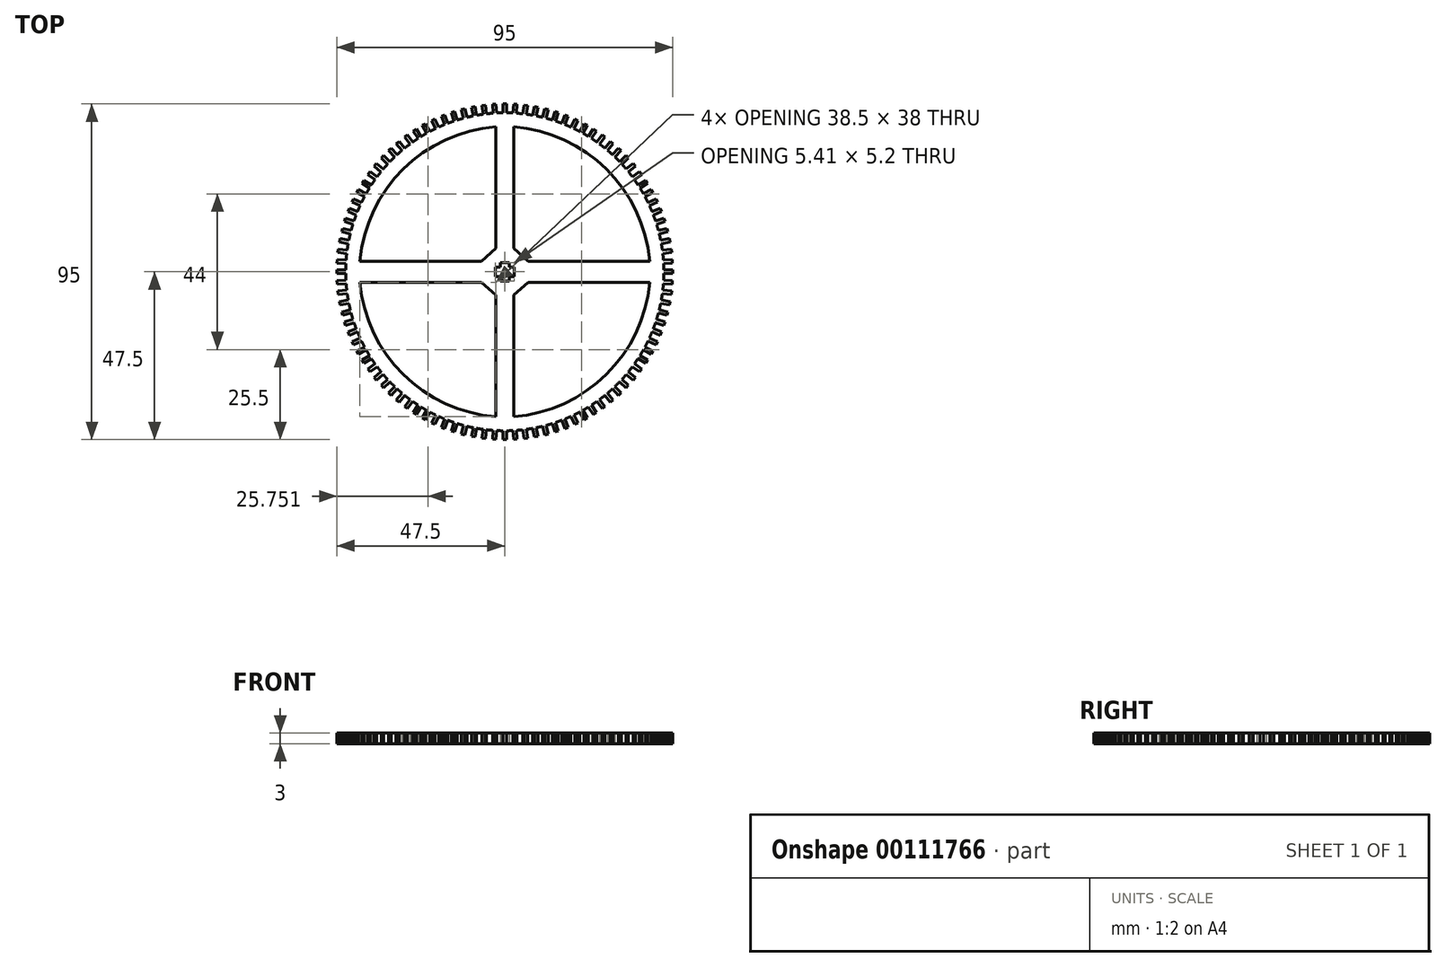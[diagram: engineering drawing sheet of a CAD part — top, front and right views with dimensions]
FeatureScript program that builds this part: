
annotation { "Feature Type Name" : "Feature", "Feature Type Description" : "" }
export const myFeature = defineFeature(function(context is Context, id is Id, definition is map)
    precondition{}
    {
        {
            var Q0;
            Q0=qCreatedBy(makeId("Top.planeOp"),FACE);
            var sketch = newSketch(context, id + "F0", { "sketchPlane" : qUnion([Q0])});
            skArc(sketch, "E0", {"start": v(-45, 0.5) * mm, "mid": v(-0.5, -45) * mm, "end": v(45, -0.5) * mm});
            skLineSegment(sketch, "E1.2.25.0", {"start": v(-47.5, 0.5) * mm, "end": v(-45, 0.5) * mm});
            skLineSegment(sketch, "E1.3.25.0", {"start": v(-47.5, -0.5) * mm, "end": v(-45, -0.5) * mm});
            skLineSegment(sketch, "E1.6.25.0", {"start": v(-47.5, 0) * mm, "end": v(-47.5, -0.5) * mm});
            skLineSegment(sketch, "E1.9.25.0", {"start": v(-47.5, 0) * mm, "end": v(-47.5, 0.5) * mm});
            skLineSegment(sketch, "E1.2.26.0", {"start": v(-47.44, -2.48) * mm, "end": v(-44.94, -2.33) * mm});
            skLineSegment(sketch, "E1.3.26.0", {"start": v(-47.37, -3.48) * mm, "end": v(-44.88, -3.32) * mm});
            skLineSegment(sketch, "E1.6.26.0", {"start": v(-47.4, -2.98) * mm, "end": v(-47.37, -3.48) * mm});
            skLineSegment(sketch, "E1.9.26.0", {"start": v(-47.4, -2.98) * mm, "end": v(-47.44, -2.48) * mm});
            skLineSegment(sketch, "E1.2.27.0", {"start": v(-47.19, -5.46) * mm, "end": v(-44.7, -5.14) * mm});
            skLineSegment(sketch, "E1.3.27.0", {"start": v(-47.06, -6.45) * mm, "end": v(-44.58, -6.14) * mm});
            skLineSegment(sketch, "E1.6.27.0", {"start": v(-47.13, -5.95) * mm, "end": v(-47.06, -6.45) * mm});
            skLineSegment(sketch, "E1.9.27.0", {"start": v(-47.13, -5.95) * mm, "end": v(-47.19, -5.46) * mm});
            skLineSegment(sketch, "E1.2.28.0", {"start": v(-46.75, -8.4) * mm, "end": v(-44.3, -7.94) * mm});
            skLineSegment(sketch, "E1.3.28.0", {"start": v(-46.56, -9.4) * mm, "end": v(-44.1, -8.92) * mm});
            skLineSegment(sketch, "E1.6.28.0", {"start": v(-46.66, -8.9) * mm, "end": v(-46.56, -9.4) * mm});
            skLineSegment(sketch, "E1.9.28.0", {"start": v(-46.66, -8.9) * mm, "end": v(-46.75, -8.4) * mm});
            skLineSegment(sketch, "E1.2.29.0", {"start": v(-46.13, -11.33) * mm, "end": v(-43.7, -10.7) * mm});
            skLineSegment(sketch, "E1.3.29.0", {"start": v(-45.88, -12.3) * mm, "end": v(-43.46, -11.67) * mm});
            skLineSegment(sketch, "E1.6.29.0", {"start": v(-46, -11.81) * mm, "end": v(-45.88, -12.3) * mm});
            skLineSegment(sketch, "E1.9.29.0", {"start": v(-46, -11.81) * mm, "end": v(-46.13, -11.33) * mm});
            skLineSegment(sketch, "E1.2.30.0", {"start": v(-45.33, -14.2) * mm, "end": v(-42.95, -13.43) * mm});
            skLineSegment(sketch, "E1.3.30.0", {"start": v(-45.02, -15.15) * mm, "end": v(-42.64, -14.38) * mm});
            skLineSegment(sketch, "E1.6.30.0", {"start": v(-45.18, -14.68) * mm, "end": v(-45.02, -15.15) * mm});
            skLineSegment(sketch, "E1.9.30.0", {"start": v(-45.18, -14.68) * mm, "end": v(-45.33, -14.2) * mm});
            skLineSegment(sketch, "E1.2.31.0", {"start": v(-44.35, -17.02) * mm, "end": v(-42.02, -16.1) * mm});
            skLineSegment(sketch, "E1.3.31.0", {"start": v(-43.98, -17.95) * mm, "end": v(-41.65, -17.03) * mm});
            skLineSegment(sketch, "E1.6.31.0", {"start": v(-44.16, -17.49) * mm, "end": v(-43.98, -17.95) * mm});
            skLineSegment(sketch, "E1.9.31.0", {"start": v(-44.16, -17.49) * mm, "end": v(-44.35, -17.02) * mm});
            skLineSegment(sketch, "E1.2.32.0", {"start": v(-43.2, -19.77) * mm, "end": v(-40.93, -18.7) * mm});
            skLineSegment(sketch, "E1.3.32.0", {"start": v(-42.77, -20.68) * mm, "end": v(-40.5, -19.61) * mm});
            skLineSegment(sketch, "E1.6.32.0", {"start": v(-42.98, -20.22) * mm, "end": v(-42.77, -20.68) * mm});
            skLineSegment(sketch, "E1.9.32.0", {"start": v(-42.98, -20.22) * mm, "end": v(-43.2, -19.77) * mm});
            skLineSegment(sketch, "E1.2.33.0", {"start": v(-41.87, -22.45) * mm, "end": v(-39.67, -21.24) * mm});
            skLineSegment(sketch, "E1.3.33.0", {"start": v(-41.38, -23.32) * mm, "end": v(-39.2, -22.12) * mm});
            skLineSegment(sketch, "E1.6.33.0", {"start": v(-41.62, -22.88) * mm, "end": v(-41.38, -23.32) * mm});
            skLineSegment(sketch, "E1.9.33.0", {"start": v(-41.62, -22.88) * mm, "end": v(-41.87, -22.45) * mm});
            skLineSegment(sketch, "E1.2.34.0", {"start": v(-40.37, -25.03) * mm, "end": v(-38.26, -23.69) * mm});
            skLineSegment(sketch, "E1.3.34.0", {"start": v(-39.84, -25.87) * mm, "end": v(-37.72, -24.53) * mm});
            skLineSegment(sketch, "E1.6.34.0", {"start": v(-40.1, -25.45) * mm, "end": v(-39.84, -25.87) * mm});
            skLineSegment(sketch, "E1.9.34.0", {"start": v(-40.1, -25.45) * mm, "end": v(-40.37, -25.03) * mm});
            skLineSegment(sketch, "E1.2.35.0", {"start": v(-38.72, -27.52) * mm, "end": v(-36.7, -26.04) * mm});
            skLineSegment(sketch, "E1.3.35.0", {"start": v(-38.13, -28.32) * mm, "end": v(-36.1, -26.85) * mm});
            skLineSegment(sketch, "E1.6.35.0", {"start": v(-38.43, -27.92) * mm, "end": v(-38.13, -28.32) * mm});
            skLineSegment(sketch, "E1.9.35.0", {"start": v(-38.43, -27.92) * mm, "end": v(-38.72, -27.52) * mm});
            skLineSegment(sketch, "E1.2.36.0", {"start": v(-36.92, -29.9) * mm, "end": v(-34.99, -28.3) * mm});
            skLineSegment(sketch, "E1.3.36.0", {"start": v(-36.28, -30.66) * mm, "end": v(-34.35, -29.07) * mm});
            skLineSegment(sketch, "E1.6.36.0", {"start": v(-36.6, -30.28) * mm, "end": v(-36.28, -30.66) * mm});
            skLineSegment(sketch, "E1.9.36.0", {"start": v(-36.6, -30.28) * mm, "end": v(-36.92, -29.9) * mm});
            skLineSegment(sketch, "E1.2.37.0", {"start": v(-34.97, -32.15) * mm, "end": v(-33.14, -30.44) * mm});
            skLineSegment(sketch, "E1.3.37.0", {"start": v(-34.28, -32.88) * mm, "end": v(-32.46, -31.17) * mm});
            skLineSegment(sketch, "E1.6.37.0", {"start": v(-34.63, -32.52) * mm, "end": v(-34.28, -32.88) * mm});
            skLineSegment(sketch, "E1.9.37.0", {"start": v(-34.63, -32.52) * mm, "end": v(-34.97, -32.15) * mm});
            skLineSegment(sketch, "E1.2.38.0", {"start": v(-32.88, -34.28) * mm, "end": v(-31.17, -32.46) * mm});
            skLineSegment(sketch, "E1.3.38.0", {"start": v(-32.15, -34.97) * mm, "end": v(-30.44, -33.14) * mm});
            skLineSegment(sketch, "E1.6.38.0", {"start": v(-32.52, -34.63) * mm, "end": v(-32.15, -34.97) * mm});
            skLineSegment(sketch, "E1.9.38.0", {"start": v(-32.52, -34.63) * mm, "end": v(-32.88, -34.28) * mm});
            skLineSegment(sketch, "E1.2.39.0", {"start": v(-30.66, -36.28) * mm, "end": v(-29.07, -34.35) * mm});
            skLineSegment(sketch, "E1.3.39.0", {"start": v(-29.9, -36.92) * mm, "end": v(-28.3, -34.99) * mm});
            skLineSegment(sketch, "E1.6.39.0", {"start": v(-30.28, -36.6) * mm, "end": v(-29.9, -36.92) * mm});
            skLineSegment(sketch, "E1.9.39.0", {"start": v(-30.28, -36.6) * mm, "end": v(-30.66, -36.28) * mm});
            skLineSegment(sketch, "E1.2.40.0", {"start": v(-28.32, -38.13) * mm, "end": v(-26.85, -36.1) * mm});
            skLineSegment(sketch, "E1.3.40.0", {"start": v(-27.52, -38.72) * mm, "end": v(-26.04, -36.7) * mm});
            skLineSegment(sketch, "E1.6.40.0", {"start": v(-27.92, -38.43) * mm, "end": v(-27.52, -38.72) * mm});
            skLineSegment(sketch, "E1.9.40.0", {"start": v(-27.92, -38.43) * mm, "end": v(-28.32, -38.13) * mm});
            skLineSegment(sketch, "E1.2.41.0", {"start": v(-25.87, -39.84) * mm, "end": v(-24.53, -37.72) * mm});
            skLineSegment(sketch, "E1.3.41.0", {"start": v(-25.03, -40.37) * mm, "end": v(-23.69, -38.26) * mm});
            skLineSegment(sketch, "E1.6.41.0", {"start": v(-25.45, -40.1) * mm, "end": v(-25.03, -40.37) * mm});
            skLineSegment(sketch, "E1.9.41.0", {"start": v(-25.45, -40.1) * mm, "end": v(-25.87, -39.84) * mm});
            skLineSegment(sketch, "E1.2.42.0", {"start": v(-23.32, -41.38) * mm, "end": v(-22.12, -39.2) * mm});
            skLineSegment(sketch, "E1.3.42.0", {"start": v(-22.45, -41.87) * mm, "end": v(-21.24, -39.67) * mm});
            skLineSegment(sketch, "E1.6.42.0", {"start": v(-22.88, -41.62) * mm, "end": v(-22.45, -41.87) * mm});
            skLineSegment(sketch, "E1.9.42.0", {"start": v(-22.88, -41.62) * mm, "end": v(-23.32, -41.38) * mm});
            skLineSegment(sketch, "E1.2.43.0", {"start": v(-20.68, -42.77) * mm, "end": v(-19.61, -40.5) * mm});
            skLineSegment(sketch, "E1.3.43.0", {"start": v(-19.77, -43.2) * mm, "end": v(-18.7, -40.93) * mm});
            skLineSegment(sketch, "E1.6.43.0", {"start": v(-20.22, -42.98) * mm, "end": v(-19.77, -43.2) * mm});
            skLineSegment(sketch, "E1.9.43.0", {"start": v(-20.22, -42.98) * mm, "end": v(-20.68, -42.77) * mm});
            skLineSegment(sketch, "E1.2.44.0", {"start": v(-17.95, -43.98) * mm, "end": v(-17.03, -41.65) * mm});
            skLineSegment(sketch, "E1.3.44.0", {"start": v(-17.02, -44.35) * mm, "end": v(-16.1, -42.02) * mm});
            skLineSegment(sketch, "E1.6.44.0", {"start": v(-17.49, -44.16) * mm, "end": v(-17.02, -44.35) * mm});
            skLineSegment(sketch, "E1.9.44.0", {"start": v(-17.49, -44.16) * mm, "end": v(-17.95, -43.98) * mm});
            skLineSegment(sketch, "E1.2.45.0", {"start": v(-15.15, -45.02) * mm, "end": v(-14.38, -42.64) * mm});
            skLineSegment(sketch, "E1.3.45.0", {"start": v(-14.2, -45.33) * mm, "end": v(-13.43, -42.95) * mm});
            skLineSegment(sketch, "E1.6.45.0", {"start": v(-14.68, -45.18) * mm, "end": v(-14.2, -45.33) * mm});
            skLineSegment(sketch, "E1.9.45.0", {"start": v(-14.68, -45.18) * mm, "end": v(-15.15, -45.02) * mm});
            skLineSegment(sketch, "E1.2.46.0", {"start": v(-12.3, -45.88) * mm, "end": v(-11.67, -43.46) * mm});
            skLineSegment(sketch, "E1.3.46.0", {"start": v(-11.33, -46.13) * mm, "end": v(-10.7, -43.7) * mm});
            skLineSegment(sketch, "E1.6.46.0", {"start": v(-11.81, -46) * mm, "end": v(-11.33, -46.13) * mm});
            skLineSegment(sketch, "E1.9.46.0", {"start": v(-11.81, -46) * mm, "end": v(-12.3, -45.88) * mm});
            skLineSegment(sketch, "E1.2.47.0", {"start": v(-9.4, -46.56) * mm, "end": v(-8.92, -44.1) * mm});
            skLineSegment(sketch, "E1.3.47.0", {"start": v(-8.4, -46.75) * mm, "end": v(-7.94, -44.3) * mm});
            skLineSegment(sketch, "E1.6.47.0", {"start": v(-8.9, -46.66) * mm, "end": v(-8.4, -46.75) * mm});
            skLineSegment(sketch, "E1.9.47.0", {"start": v(-8.9, -46.66) * mm, "end": v(-9.4, -46.56) * mm});
            skLineSegment(sketch, "E1.2.48.0", {"start": v(-6.45, -47.06) * mm, "end": v(-6.14, -44.58) * mm});
            skLineSegment(sketch, "E1.3.48.0", {"start": v(-5.46, -47.19) * mm, "end": v(-5.14, -44.7) * mm});
            skLineSegment(sketch, "E1.6.48.0", {"start": v(-5.95, -47.13) * mm, "end": v(-5.46, -47.19) * mm});
            skLineSegment(sketch, "E1.9.48.0", {"start": v(-5.95, -47.13) * mm, "end": v(-6.45, -47.06) * mm});
            skLineSegment(sketch, "E1.2.49.0", {"start": v(-3.48, -47.37) * mm, "end": v(-3.32, -44.88) * mm});
            skLineSegment(sketch, "E1.3.49.0", {"start": v(-2.48, -47.44) * mm, "end": v(-2.33, -44.94) * mm});
            skLineSegment(sketch, "E1.6.49.0", {"start": v(-2.98, -47.4) * mm, "end": v(-2.48, -47.44) * mm});
            skLineSegment(sketch, "E1.9.49.0", {"start": v(-2.98, -47.4) * mm, "end": v(-3.48, -47.37) * mm});
            skLineSegment(sketch, "E1.2.50.0", {"start": v(-0.5, -47.5) * mm, "end": v(-0.5, -45) * mm});
            skLineSegment(sketch, "E1.3.50.0", {"start": v(0.5, -47.5) * mm, "end": v(0.5, -45) * mm});
            skLineSegment(sketch, "E1.6.50.0", {"start": v(0, -47.5) * mm, "end": v(0.5, -47.5) * mm});
            skLineSegment(sketch, "E1.9.50.0", {"start": v(0, -47.5) * mm, "end": v(-0.5, -47.5) * mm});
            skLineSegment(sketch, "E1.2.51.0", {"start": v(2.48, -47.44) * mm, "end": v(2.33, -44.94) * mm});
            skLineSegment(sketch, "E1.3.51.0", {"start": v(3.48, -47.37) * mm, "end": v(3.32, -44.88) * mm});
            skLineSegment(sketch, "E1.6.51.0", {"start": v(2.98, -47.4) * mm, "end": v(3.48, -47.37) * mm});
            skLineSegment(sketch, "E1.9.51.0", {"start": v(2.98, -47.4) * mm, "end": v(2.48, -47.44) * mm});
            skLineSegment(sketch, "E1.2.52.0", {"start": v(5.46, -47.19) * mm, "end": v(5.14, -44.7) * mm});
            skLineSegment(sketch, "E1.3.52.0", {"start": v(6.45, -47.06) * mm, "end": v(6.14, -44.58) * mm});
            skLineSegment(sketch, "E1.6.52.0", {"start": v(5.95, -47.13) * mm, "end": v(6.45, -47.06) * mm});
            skLineSegment(sketch, "E1.9.52.0", {"start": v(5.95, -47.13) * mm, "end": v(5.46, -47.19) * mm});
            skLineSegment(sketch, "E1.2.53.0", {"start": v(8.4, -46.75) * mm, "end": v(7.94, -44.3) * mm});
            skLineSegment(sketch, "E1.3.53.0", {"start": v(9.4, -46.56) * mm, "end": v(8.92, -44.1) * mm});
            skLineSegment(sketch, "E1.6.53.0", {"start": v(8.9, -46.66) * mm, "end": v(9.4, -46.56) * mm});
            skLineSegment(sketch, "E1.9.53.0", {"start": v(8.9, -46.66) * mm, "end": v(8.4, -46.75) * mm});
            skLineSegment(sketch, "E1.2.54.0", {"start": v(11.33, -46.13) * mm, "end": v(10.7, -43.7) * mm});
            skLineSegment(sketch, "E1.3.54.0", {"start": v(12.3, -45.88) * mm, "end": v(11.67, -43.46) * mm});
            skLineSegment(sketch, "E1.6.54.0", {"start": v(11.81, -46) * mm, "end": v(12.3, -45.88) * mm});
            skLineSegment(sketch, "E1.9.54.0", {"start": v(11.81, -46) * mm, "end": v(11.33, -46.13) * mm});
            skLineSegment(sketch, "E1.2.55.0", {"start": v(14.2, -45.33) * mm, "end": v(13.43, -42.95) * mm});
            skLineSegment(sketch, "E1.3.55.0", {"start": v(15.15, -45.02) * mm, "end": v(14.38, -42.64) * mm});
            skLineSegment(sketch, "E1.6.55.0", {"start": v(14.68, -45.18) * mm, "end": v(15.15, -45.02) * mm});
            skLineSegment(sketch, "E1.9.55.0", {"start": v(14.68, -45.18) * mm, "end": v(14.2, -45.33) * mm});
            skLineSegment(sketch, "E1.2.56.0", {"start": v(17.02, -44.35) * mm, "end": v(16.1, -42.02) * mm});
            skLineSegment(sketch, "E1.3.56.0", {"start": v(17.95, -43.98) * mm, "end": v(17.03, -41.65) * mm});
            skLineSegment(sketch, "E1.6.56.0", {"start": v(17.49, -44.16) * mm, "end": v(17.95, -43.98) * mm});
            skLineSegment(sketch, "E1.9.56.0", {"start": v(17.49, -44.16) * mm, "end": v(17.02, -44.35) * mm});
            skLineSegment(sketch, "E1.2.57.0", {"start": v(19.77, -43.2) * mm, "end": v(18.7, -40.93) * mm});
            skLineSegment(sketch, "E1.3.57.0", {"start": v(20.68, -42.77) * mm, "end": v(19.61, -40.5) * mm});
            skLineSegment(sketch, "E1.6.57.0", {"start": v(20.22, -42.98) * mm, "end": v(20.68, -42.77) * mm});
            skLineSegment(sketch, "E1.9.57.0", {"start": v(20.22, -42.98) * mm, "end": v(19.77, -43.2) * mm});
            skLineSegment(sketch, "E1.2.58.0", {"start": v(22.45, -41.87) * mm, "end": v(21.24, -39.67) * mm});
            skLineSegment(sketch, "E1.3.58.0", {"start": v(23.32, -41.38) * mm, "end": v(22.12, -39.2) * mm});
            skLineSegment(sketch, "E1.6.58.0", {"start": v(22.88, -41.62) * mm, "end": v(23.32, -41.38) * mm});
            skLineSegment(sketch, "E1.9.58.0", {"start": v(22.88, -41.62) * mm, "end": v(22.45, -41.87) * mm});
            skLineSegment(sketch, "E1.2.59.0", {"start": v(25.03, -40.37) * mm, "end": v(23.69, -38.26) * mm});
            skLineSegment(sketch, "E1.3.59.0", {"start": v(25.87, -39.84) * mm, "end": v(24.53, -37.72) * mm});
            skLineSegment(sketch, "E1.6.59.0", {"start": v(25.45, -40.1) * mm, "end": v(25.87, -39.84) * mm});
            skLineSegment(sketch, "E1.9.59.0", {"start": v(25.45, -40.1) * mm, "end": v(25.03, -40.37) * mm});
            skLineSegment(sketch, "E1.2.60.0", {"start": v(27.52, -38.72) * mm, "end": v(26.04, -36.7) * mm});
            skLineSegment(sketch, "E1.3.60.0", {"start": v(28.32, -38.13) * mm, "end": v(26.85, -36.1) * mm});
            skLineSegment(sketch, "E1.6.60.0", {"start": v(27.92, -38.43) * mm, "end": v(28.32, -38.13) * mm});
            skLineSegment(sketch, "E1.9.60.0", {"start": v(27.92, -38.43) * mm, "end": v(27.52, -38.72) * mm});
            skLineSegment(sketch, "E1.2.61.0", {"start": v(29.9, -36.92) * mm, "end": v(28.3, -34.99) * mm});
            skLineSegment(sketch, "E1.3.61.0", {"start": v(30.66, -36.28) * mm, "end": v(29.07, -34.35) * mm});
            skLineSegment(sketch, "E1.6.61.0", {"start": v(30.28, -36.6) * mm, "end": v(30.66, -36.28) * mm});
            skLineSegment(sketch, "E1.9.61.0", {"start": v(30.28, -36.6) * mm, "end": v(29.9, -36.92) * mm});
            skLineSegment(sketch, "E1.2.62.0", {"start": v(32.15, -34.97) * mm, "end": v(30.44, -33.14) * mm});
            skLineSegment(sketch, "E1.3.62.0", {"start": v(32.88, -34.28) * mm, "end": v(31.17, -32.46) * mm});
            skLineSegment(sketch, "E1.6.62.0", {"start": v(32.52, -34.63) * mm, "end": v(32.88, -34.28) * mm});
            skLineSegment(sketch, "E1.9.62.0", {"start": v(32.52, -34.63) * mm, "end": v(32.15, -34.97) * mm});
            skLineSegment(sketch, "E1.2.63.0", {"start": v(34.28, -32.88) * mm, "end": v(32.46, -31.17) * mm});
            skLineSegment(sketch, "E1.3.63.0", {"start": v(34.97, -32.15) * mm, "end": v(33.14, -30.44) * mm});
            skLineSegment(sketch, "E1.6.63.0", {"start": v(34.63, -32.52) * mm, "end": v(34.97, -32.15) * mm});
            skLineSegment(sketch, "E1.9.63.0", {"start": v(34.63, -32.52) * mm, "end": v(34.28, -32.88) * mm});
            skLineSegment(sketch, "E1.2.64.0", {"start": v(36.28, -30.66) * mm, "end": v(34.35, -29.07) * mm});
            skLineSegment(sketch, "E1.3.64.0", {"start": v(36.92, -29.9) * mm, "end": v(34.99, -28.3) * mm});
            skLineSegment(sketch, "E1.6.64.0", {"start": v(36.6, -30.28) * mm, "end": v(36.92, -29.9) * mm});
            skLineSegment(sketch, "E1.9.64.0", {"start": v(36.6, -30.28) * mm, "end": v(36.28, -30.66) * mm});
            skLineSegment(sketch, "E1.2.65.0", {"start": v(38.13, -28.32) * mm, "end": v(36.1, -26.85) * mm});
            skLineSegment(sketch, "E1.3.65.0", {"start": v(38.72, -27.52) * mm, "end": v(36.7, -26.04) * mm});
            skLineSegment(sketch, "E1.6.65.0", {"start": v(38.43, -27.92) * mm, "end": v(38.72, -27.52) * mm});
            skLineSegment(sketch, "E1.9.65.0", {"start": v(38.43, -27.92) * mm, "end": v(38.13, -28.32) * mm});
            skLineSegment(sketch, "E1.2.66.0", {"start": v(39.84, -25.87) * mm, "end": v(37.72, -24.53) * mm});
            skLineSegment(sketch, "E1.3.66.0", {"start": v(40.37, -25.03) * mm, "end": v(38.26, -23.69) * mm});
            skLineSegment(sketch, "E1.6.66.0", {"start": v(40.1, -25.45) * mm, "end": v(40.37, -25.03) * mm});
            skLineSegment(sketch, "E1.9.66.0", {"start": v(40.1, -25.45) * mm, "end": v(39.84, -25.87) * mm});
            skLineSegment(sketch, "E1.2.67.0", {"start": v(41.38, -23.32) * mm, "end": v(39.2, -22.12) * mm});
            skLineSegment(sketch, "E1.3.67.0", {"start": v(41.87, -22.45) * mm, "end": v(39.67, -21.24) * mm});
            skLineSegment(sketch, "E1.6.67.0", {"start": v(41.62, -22.88) * mm, "end": v(41.87, -22.45) * mm});
            skLineSegment(sketch, "E1.9.67.0", {"start": v(41.62, -22.88) * mm, "end": v(41.38, -23.32) * mm});
            skLineSegment(sketch, "E1.2.68.0", {"start": v(42.77, -20.68) * mm, "end": v(40.5, -19.61) * mm});
            skLineSegment(sketch, "E1.3.68.0", {"start": v(43.2, -19.77) * mm, "end": v(40.93, -18.7) * mm});
            skLineSegment(sketch, "E1.6.68.0", {"start": v(42.98, -20.22) * mm, "end": v(43.2, -19.77) * mm});
            skLineSegment(sketch, "E1.9.68.0", {"start": v(42.98, -20.22) * mm, "end": v(42.77, -20.68) * mm});
            skLineSegment(sketch, "E1.2.69.0", {"start": v(43.98, -17.95) * mm, "end": v(41.65, -17.03) * mm});
            skLineSegment(sketch, "E1.3.69.0", {"start": v(44.35, -17.02) * mm, "end": v(42.02, -16.1) * mm});
            skLineSegment(sketch, "E1.6.69.0", {"start": v(44.16, -17.49) * mm, "end": v(44.35, -17.02) * mm});
            skLineSegment(sketch, "E1.9.69.0", {"start": v(44.16, -17.49) * mm, "end": v(43.98, -17.95) * mm});
            skLineSegment(sketch, "E1.2.70.0", {"start": v(45.02, -15.15) * mm, "end": v(42.64, -14.38) * mm});
            skLineSegment(sketch, "E1.3.70.0", {"start": v(45.33, -14.2) * mm, "end": v(42.95, -13.43) * mm});
            skLineSegment(sketch, "E1.6.70.0", {"start": v(45.18, -14.68) * mm, "end": v(45.33, -14.2) * mm});
            skLineSegment(sketch, "E1.9.70.0", {"start": v(45.18, -14.68) * mm, "end": v(45.02, -15.15) * mm});
            skLineSegment(sketch, "E1.2.71.0", {"start": v(45.88, -12.3) * mm, "end": v(43.46, -11.67) * mm});
            skLineSegment(sketch, "E1.3.71.0", {"start": v(46.13, -11.33) * mm, "end": v(43.7, -10.7) * mm});
            skLineSegment(sketch, "E1.6.71.0", {"start": v(46, -11.81) * mm, "end": v(46.13, -11.33) * mm});
            skLineSegment(sketch, "E1.9.71.0", {"start": v(46, -11.81) * mm, "end": v(45.88, -12.3) * mm});
            skLineSegment(sketch, "E1.2.72.0", {"start": v(46.56, -9.4) * mm, "end": v(44.1, -8.92) * mm});
            skLineSegment(sketch, "E1.3.72.0", {"start": v(46.75, -8.4) * mm, "end": v(44.3, -7.94) * mm});
            skLineSegment(sketch, "E1.6.72.0", {"start": v(46.66, -8.9) * mm, "end": v(46.75, -8.4) * mm});
            skLineSegment(sketch, "E1.9.72.0", {"start": v(46.66, -8.9) * mm, "end": v(46.56, -9.4) * mm});
            skLineSegment(sketch, "E1.2.73.0", {"start": v(47.06, -6.45) * mm, "end": v(44.58, -6.14) * mm});
            skLineSegment(sketch, "E1.3.73.0", {"start": v(47.19, -5.46) * mm, "end": v(44.7, -5.14) * mm});
            skLineSegment(sketch, "E1.6.73.0", {"start": v(47.13, -5.95) * mm, "end": v(47.19, -5.46) * mm});
            skLineSegment(sketch, "E1.9.73.0", {"start": v(47.13, -5.95) * mm, "end": v(47.06, -6.45) * mm});
            skLineSegment(sketch, "E1.2.74.0", {"start": v(47.37, -3.48) * mm, "end": v(44.88, -3.32) * mm});
            skLineSegment(sketch, "E1.3.74.0", {"start": v(47.44, -2.48) * mm, "end": v(44.94, -2.33) * mm});
            skLineSegment(sketch, "E1.6.74.0", {"start": v(47.4, -2.98) * mm, "end": v(47.44, -2.48) * mm});
            skLineSegment(sketch, "E1.9.74.0", {"start": v(47.4, -2.98) * mm, "end": v(47.37, -3.48) * mm});
            skLineSegment(sketch, "E2.MirrorCS", {"start": v(-6.6, -3) * mm, "end": v(-41, -3) * mm});
            skLineSegment(sketch, "E3.MirrorCS", {"start": v(-2.5, -6.6) * mm, "end": v(-6.6, -3) * mm});
            skLineSegment(sketch, "E4.MirrorCS", {"start": v(-2.5, -6.6) * mm, "end": v(-2.5, -41) * mm});
            skArc(sketch, "E5.MirrorCS", {"start": v(-41, -3) * mm, "mid": v(-28.72, -29.07) * mm, "end": v(-2.5, -41) * mm});
            skLineSegment(sketch, "E6.MirrorCS", {"start": v(2.5, -6.6) * mm, "end": v(2.5, -41) * mm});
            skLineSegment(sketch, "E7.MirrorCS", {"start": v(2.5, -6.6) * mm, "end": v(6.6, -3) * mm});
            skLineSegment(sketch, "E8.MirrorCS", {"start": v(6.6, -3) * mm, "end": v(41, -3) * mm});
            skArc(sketch, "E9.MirrorCS", {"start": v(41, -3) * mm, "mid": v(28.72, -29.07) * mm, "end": v(2.5, -41) * mm});
            skArc(sketch, "E10", {"start": v(-4, 0) * mm, "mid": v(0, -4) * mm, "end": v(4, 0) * mm});
            skLineSegment(sketch, "E11", {"start": v(-4, 0) * mm, "end": v(-16, 0) * mm});
            skLineSegment(sketch, "E12", {"start": v(-16, 0) * mm, "end": v(-15.27, -1.74) * mm});
            skLineSegment(sketch, "E13", {"start": v(-15.27, -1.74) * mm, "end": v(-26.47, -1.74) * mm});
            skLineSegment(sketch, "E14", {"start": v(-45, 0.5) * mm, "end": v(-25.37, 0) * mm});
            skLineSegment(sketch, "E15", {"start": v(-25.37, 0) * mm, "end": v(-26.47, -1.74) * mm});
            skLineSegment(sketch, "E16", {"start": v(45, -0.5) * mm, "end": v(34.22, 0) * mm});
            skLineSegment(sketch, "E17", {"start": v(34.22, 0) * mm, "end": v(35.03, -1.4) * mm});
            skLineSegment(sketch, "E18", {"start": v(35.03, -1.4) * mm, "end": v(24.89, -1.4) * mm});
            skLineSegment(sketch, "E19", {"start": v(24.89, -1.4) * mm, "end": v(26.1, 0) * mm});
            skLineSegment(sketch, "E20", {"start": v(26.1, 0) * mm, "end": v(4, 0) * mm});
            skCircle(sketch, "E21", {"center": v(0, 0) * mm, "radius": 45 * mm});
            skLineSegment(sketch, "E22.MirrorCS", {"start": v(-6.6, 3) * mm, "end": v(-41, 3) * mm});
            skLineSegment(sketch, "E23.MirrorCS", {"start": v(-2.5, 6.6) * mm, "end": v(-6.6, 3) * mm});
            skLineSegment(sketch, "E24.MirrorCS", {"start": v(-2.5, 6.6) * mm, "end": v(-2.5, 41) * mm});
            skArc(sketch, "E25.MirrorCS", {"start": v(-41, 3) * mm, "mid": v(-28.72, 29.07) * mm, "end": v(-2.5, 41) * mm});
            skLineSegment(sketch, "E26.MirrorCS", {"start": v(2.5, 6.6) * mm, "end": v(2.5, 41) * mm});
            skArc(sketch, "E27.MirrorCS", {"start": v(41, 3) * mm, "mid": v(28.72, 29.07) * mm, "end": v(2.5, 41) * mm});
            skLineSegment(sketch, "E28.MirrorCS", {"start": v(6.6, 3) * mm, "end": v(41, 3) * mm});
            skLineSegment(sketch, "E29.MirrorCS", {"start": v(2.5, 6.6) * mm, "end": v(6.6, 3) * mm});
            skLineSegment(sketch, "E30.1.50.0", {"start": v(47.5, 0.5) * mm, "end": v(45, 0.5) * mm});
            skLineSegment(sketch, "E30.3.50.0", {"start": v(47.5, -0.5) * mm, "end": v(45, -0.5) * mm});
            skLineSegment(sketch, "E30.6.50.0", {"start": v(47.5, 0) * mm, "end": v(47.5, -0.5) * mm});
            skLineSegment(sketch, "E30.9.50.0", {"start": v(47.5, 0) * mm, "end": v(47.5, 0.5) * mm});
            skLineSegment(sketch, "E30.1.51.0", {"start": v(47.37, 3.48) * mm, "end": v(44.88, 3.32) * mm});
            skLineSegment(sketch, "E30.3.51.0", {"start": v(47.44, 2.48) * mm, "end": v(44.94, 2.33) * mm});
            skLineSegment(sketch, "E30.6.51.0", {"start": v(47.4, 2.98) * mm, "end": v(47.44, 2.48) * mm});
            skLineSegment(sketch, "E30.9.51.0", {"start": v(47.4, 2.98) * mm, "end": v(47.37, 3.48) * mm});
            skLineSegment(sketch, "E30.1.52.0", {"start": v(47.06, 6.45) * mm, "end": v(44.58, 6.14) * mm});
            skLineSegment(sketch, "E30.3.52.0", {"start": v(47.19, 5.46) * mm, "end": v(44.7, 5.14) * mm});
            skLineSegment(sketch, "E30.6.52.0", {"start": v(47.13, 5.95) * mm, "end": v(47.19, 5.46) * mm});
            skLineSegment(sketch, "E30.9.52.0", {"start": v(47.13, 5.95) * mm, "end": v(47.06, 6.45) * mm});
            skLineSegment(sketch, "E30.1.53.0", {"start": v(46.56, 9.4) * mm, "end": v(44.1, 8.92) * mm});
            skLineSegment(sketch, "E30.3.53.0", {"start": v(46.75, 8.4) * mm, "end": v(44.3, 7.94) * mm});
            skLineSegment(sketch, "E30.6.53.0", {"start": v(46.66, 8.9) * mm, "end": v(46.75, 8.4) * mm});
            skLineSegment(sketch, "E30.9.53.0", {"start": v(46.66, 8.9) * mm, "end": v(46.56, 9.4) * mm});
            skLineSegment(sketch, "E30.1.54.0", {"start": v(45.88, 12.3) * mm, "end": v(43.46, 11.67) * mm});
            skLineSegment(sketch, "E30.3.54.0", {"start": v(46.13, 11.33) * mm, "end": v(43.7, 10.7) * mm});
            skLineSegment(sketch, "E30.6.54.0", {"start": v(46, 11.81) * mm, "end": v(46.13, 11.33) * mm});
            skLineSegment(sketch, "E30.9.54.0", {"start": v(46, 11.81) * mm, "end": v(45.88, 12.3) * mm});
            skLineSegment(sketch, "E30.1.55.0", {"start": v(45.02, 15.15) * mm, "end": v(42.64, 14.38) * mm});
            skLineSegment(sketch, "E30.3.55.0", {"start": v(45.33, 14.2) * mm, "end": v(42.95, 13.43) * mm});
            skLineSegment(sketch, "E30.6.55.0", {"start": v(45.18, 14.68) * mm, "end": v(45.33, 14.2) * mm});
            skLineSegment(sketch, "E30.9.55.0", {"start": v(45.18, 14.68) * mm, "end": v(45.02, 15.15) * mm});
            skLineSegment(sketch, "E30.1.56.0", {"start": v(43.98, 17.95) * mm, "end": v(41.65, 17.03) * mm});
            skLineSegment(sketch, "E30.3.56.0", {"start": v(44.35, 17.02) * mm, "end": v(42.02, 16.1) * mm});
            skLineSegment(sketch, "E30.6.56.0", {"start": v(44.16, 17.49) * mm, "end": v(44.35, 17.02) * mm});
            skLineSegment(sketch, "E30.9.56.0", {"start": v(44.16, 17.49) * mm, "end": v(43.98, 17.95) * mm});
            skLineSegment(sketch, "E30.1.57.0", {"start": v(42.77, 20.68) * mm, "end": v(40.5, 19.61) * mm});
            skLineSegment(sketch, "E30.3.57.0", {"start": v(43.2, 19.77) * mm, "end": v(40.93, 18.7) * mm});
            skLineSegment(sketch, "E30.6.57.0", {"start": v(42.98, 20.22) * mm, "end": v(43.2, 19.77) * mm});
            skLineSegment(sketch, "E30.9.57.0", {"start": v(42.98, 20.22) * mm, "end": v(42.77, 20.68) * mm});
            skLineSegment(sketch, "E30.1.58.0", {"start": v(41.38, 23.32) * mm, "end": v(39.2, 22.12) * mm});
            skLineSegment(sketch, "E30.3.58.0", {"start": v(41.87, 22.45) * mm, "end": v(39.67, 21.24) * mm});
            skLineSegment(sketch, "E30.6.58.0", {"start": v(41.62, 22.88) * mm, "end": v(41.87, 22.45) * mm});
            skLineSegment(sketch, "E30.9.58.0", {"start": v(41.62, 22.88) * mm, "end": v(41.38, 23.32) * mm});
            skLineSegment(sketch, "E30.1.59.0", {"start": v(39.84, 25.87) * mm, "end": v(37.72, 24.53) * mm});
            skLineSegment(sketch, "E30.3.59.0", {"start": v(40.37, 25.03) * mm, "end": v(38.26, 23.69) * mm});
            skLineSegment(sketch, "E30.6.59.0", {"start": v(40.1, 25.45) * mm, "end": v(40.37, 25.03) * mm});
            skLineSegment(sketch, "E30.9.59.0", {"start": v(40.1, 25.45) * mm, "end": v(39.84, 25.87) * mm});
            skLineSegment(sketch, "E30.1.60.0", {"start": v(38.13, 28.32) * mm, "end": v(36.1, 26.85) * mm});
            skLineSegment(sketch, "E30.3.60.0", {"start": v(38.72, 27.52) * mm, "end": v(36.7, 26.04) * mm});
            skLineSegment(sketch, "E30.6.60.0", {"start": v(38.43, 27.92) * mm, "end": v(38.72, 27.52) * mm});
            skLineSegment(sketch, "E30.9.60.0", {"start": v(38.43, 27.92) * mm, "end": v(38.13, 28.32) * mm});
            skLineSegment(sketch, "E30.1.61.0", {"start": v(36.28, 30.66) * mm, "end": v(34.35, 29.07) * mm});
            skLineSegment(sketch, "E30.3.61.0", {"start": v(36.92, 29.9) * mm, "end": v(34.99, 28.3) * mm});
            skLineSegment(sketch, "E30.6.61.0", {"start": v(36.6, 30.28) * mm, "end": v(36.92, 29.9) * mm});
            skLineSegment(sketch, "E30.9.61.0", {"start": v(36.6, 30.28) * mm, "end": v(36.28, 30.66) * mm});
            skLineSegment(sketch, "E30.1.62.0", {"start": v(34.28, 32.88) * mm, "end": v(32.46, 31.17) * mm});
            skLineSegment(sketch, "E30.3.62.0", {"start": v(34.97, 32.15) * mm, "end": v(33.14, 30.44) * mm});
            skLineSegment(sketch, "E30.6.62.0", {"start": v(34.63, 32.52) * mm, "end": v(34.97, 32.15) * mm});
            skLineSegment(sketch, "E30.9.62.0", {"start": v(34.63, 32.52) * mm, "end": v(34.28, 32.88) * mm});
            skLineSegment(sketch, "E30.1.63.0", {"start": v(32.15, 34.97) * mm, "end": v(30.44, 33.14) * mm});
            skLineSegment(sketch, "E30.3.63.0", {"start": v(32.88, 34.28) * mm, "end": v(31.17, 32.46) * mm});
            skLineSegment(sketch, "E30.6.63.0", {"start": v(32.52, 34.63) * mm, "end": v(32.88, 34.28) * mm});
            skLineSegment(sketch, "E30.9.63.0", {"start": v(32.52, 34.63) * mm, "end": v(32.15, 34.97) * mm});
            skLineSegment(sketch, "E30.1.64.0", {"start": v(29.9, 36.92) * mm, "end": v(28.3, 34.99) * mm});
            skLineSegment(sketch, "E30.3.64.0", {"start": v(30.66, 36.28) * mm, "end": v(29.07, 34.35) * mm});
            skLineSegment(sketch, "E30.6.64.0", {"start": v(30.28, 36.6) * mm, "end": v(30.66, 36.28) * mm});
            skLineSegment(sketch, "E30.9.64.0", {"start": v(30.28, 36.6) * mm, "end": v(29.9, 36.92) * mm});
            skLineSegment(sketch, "E30.1.65.0", {"start": v(27.52, 38.72) * mm, "end": v(26.04, 36.7) * mm});
            skLineSegment(sketch, "E30.3.65.0", {"start": v(28.32, 38.13) * mm, "end": v(26.85, 36.1) * mm});
            skLineSegment(sketch, "E30.6.65.0", {"start": v(27.92, 38.43) * mm, "end": v(28.32, 38.13) * mm});
            skLineSegment(sketch, "E30.9.65.0", {"start": v(27.92, 38.43) * mm, "end": v(27.52, 38.72) * mm});
            skLineSegment(sketch, "E30.1.66.0", {"start": v(25.03, 40.37) * mm, "end": v(23.69, 38.26) * mm});
            skLineSegment(sketch, "E30.3.66.0", {"start": v(25.87, 39.84) * mm, "end": v(24.53, 37.72) * mm});
            skLineSegment(sketch, "E30.6.66.0", {"start": v(25.45, 40.1) * mm, "end": v(25.87, 39.84) * mm});
            skLineSegment(sketch, "E30.9.66.0", {"start": v(25.45, 40.1) * mm, "end": v(25.03, 40.37) * mm});
            skLineSegment(sketch, "E30.1.67.0", {"start": v(22.45, 41.87) * mm, "end": v(21.24, 39.67) * mm});
            skLineSegment(sketch, "E30.3.67.0", {"start": v(23.32, 41.38) * mm, "end": v(22.12, 39.2) * mm});
            skLineSegment(sketch, "E30.6.67.0", {"start": v(22.88, 41.62) * mm, "end": v(23.32, 41.38) * mm});
            skLineSegment(sketch, "E30.9.67.0", {"start": v(22.88, 41.62) * mm, "end": v(22.45, 41.87) * mm});
            skLineSegment(sketch, "E30.1.68.0", {"start": v(19.77, 43.2) * mm, "end": v(18.7, 40.93) * mm});
            skLineSegment(sketch, "E30.3.68.0", {"start": v(20.68, 42.77) * mm, "end": v(19.61, 40.5) * mm});
            skLineSegment(sketch, "E30.6.68.0", {"start": v(20.22, 42.98) * mm, "end": v(20.68, 42.77) * mm});
            skLineSegment(sketch, "E30.9.68.0", {"start": v(20.22, 42.98) * mm, "end": v(19.77, 43.2) * mm});
            skLineSegment(sketch, "E30.1.69.0", {"start": v(17.02, 44.35) * mm, "end": v(16.1, 42.02) * mm});
            skLineSegment(sketch, "E30.3.69.0", {"start": v(17.95, 43.98) * mm, "end": v(17.03, 41.65) * mm});
            skLineSegment(sketch, "E30.6.69.0", {"start": v(17.49, 44.16) * mm, "end": v(17.95, 43.98) * mm});
            skLineSegment(sketch, "E30.9.69.0", {"start": v(17.49, 44.16) * mm, "end": v(17.02, 44.35) * mm});
            skLineSegment(sketch, "E30.1.70.0", {"start": v(14.2, 45.33) * mm, "end": v(13.43, 42.95) * mm});
            skLineSegment(sketch, "E30.3.70.0", {"start": v(15.15, 45.02) * mm, "end": v(14.38, 42.64) * mm});
            skLineSegment(sketch, "E30.6.70.0", {"start": v(14.68, 45.18) * mm, "end": v(15.15, 45.02) * mm});
            skLineSegment(sketch, "E30.9.70.0", {"start": v(14.68, 45.18) * mm, "end": v(14.2, 45.33) * mm});
            skLineSegment(sketch, "E30.1.71.0", {"start": v(11.33, 46.13) * mm, "end": v(10.7, 43.7) * mm});
            skLineSegment(sketch, "E30.3.71.0", {"start": v(12.3, 45.88) * mm, "end": v(11.67, 43.46) * mm});
            skLineSegment(sketch, "E30.6.71.0", {"start": v(11.81, 46) * mm, "end": v(12.3, 45.88) * mm});
            skLineSegment(sketch, "E30.9.71.0", {"start": v(11.81, 46) * mm, "end": v(11.33, 46.13) * mm});
            skLineSegment(sketch, "E30.1.72.0", {"start": v(8.4, 46.75) * mm, "end": v(7.94, 44.3) * mm});
            skLineSegment(sketch, "E30.3.72.0", {"start": v(9.4, 46.56) * mm, "end": v(8.92, 44.1) * mm});
            skLineSegment(sketch, "E30.6.72.0", {"start": v(8.9, 46.66) * mm, "end": v(9.4, 46.56) * mm});
            skLineSegment(sketch, "E30.9.72.0", {"start": v(8.9, 46.66) * mm, "end": v(8.4, 46.75) * mm});
            skLineSegment(sketch, "E30.1.73.0", {"start": v(5.46, 47.19) * mm, "end": v(5.14, 44.7) * mm});
            skLineSegment(sketch, "E30.3.73.0", {"start": v(6.45, 47.06) * mm, "end": v(6.14, 44.58) * mm});
            skLineSegment(sketch, "E30.6.73.0", {"start": v(5.95, 47.13) * mm, "end": v(6.45, 47.06) * mm});
            skLineSegment(sketch, "E30.9.73.0", {"start": v(5.95, 47.13) * mm, "end": v(5.46, 47.19) * mm});
            skLineSegment(sketch, "E30.1.74.0", {"start": v(2.48, 47.44) * mm, "end": v(2.33, 44.94) * mm});
            skLineSegment(sketch, "E30.3.74.0", {"start": v(3.48, 47.37) * mm, "end": v(3.32, 44.88) * mm});
            skLineSegment(sketch, "E30.6.74.0", {"start": v(2.98, 47.4) * mm, "end": v(3.48, 47.37) * mm});
            skLineSegment(sketch, "E30.9.74.0", {"start": v(2.98, 47.4) * mm, "end": v(2.48, 47.44) * mm});
            skLineSegment(sketch, "E30.1.75.0", {"start": v(-0.5, 47.5) * mm, "end": v(-0.5, 45) * mm});
            skLineSegment(sketch, "E30.3.75.0", {"start": v(0.5, 47.5) * mm, "end": v(0.5, 45) * mm});
            skLineSegment(sketch, "E30.6.75.0", {"start": v(0, 47.5) * mm, "end": v(0.5, 47.5) * mm});
            skLineSegment(sketch, "E30.9.75.0", {"start": v(0, 47.5) * mm, "end": v(-0.5, 47.5) * mm});
            skLineSegment(sketch, "E30.1.76.0", {"start": v(-3.48, 47.37) * mm, "end": v(-3.32, 44.88) * mm});
            skLineSegment(sketch, "E30.3.76.0", {"start": v(-2.48, 47.44) * mm, "end": v(-2.33, 44.94) * mm});
            skLineSegment(sketch, "E30.6.76.0", {"start": v(-2.98, 47.4) * mm, "end": v(-2.48, 47.44) * mm});
            skLineSegment(sketch, "E30.9.76.0", {"start": v(-2.98, 47.4) * mm, "end": v(-3.48, 47.37) * mm});
            skLineSegment(sketch, "E30.1.77.0", {"start": v(-6.45, 47.06) * mm, "end": v(-6.14, 44.58) * mm});
            skLineSegment(sketch, "E30.3.77.0", {"start": v(-5.46, 47.19) * mm, "end": v(-5.14, 44.7) * mm});
            skLineSegment(sketch, "E30.6.77.0", {"start": v(-5.95, 47.13) * mm, "end": v(-5.46, 47.19) * mm});
            skLineSegment(sketch, "E30.9.77.0", {"start": v(-5.95, 47.13) * mm, "end": v(-6.45, 47.06) * mm});
            skLineSegment(sketch, "E30.1.78.0", {"start": v(-9.4, 46.56) * mm, "end": v(-8.92, 44.1) * mm});
            skLineSegment(sketch, "E30.3.78.0", {"start": v(-8.4, 46.75) * mm, "end": v(-7.94, 44.3) * mm});
            skLineSegment(sketch, "E30.6.78.0", {"start": v(-8.9, 46.66) * mm, "end": v(-8.4, 46.75) * mm});
            skLineSegment(sketch, "E30.9.78.0", {"start": v(-8.9, 46.66) * mm, "end": v(-9.4, 46.56) * mm});
            skLineSegment(sketch, "E30.1.79.0", {"start": v(-12.3, 45.88) * mm, "end": v(-11.67, 43.46) * mm});
            skLineSegment(sketch, "E30.3.79.0", {"start": v(-11.33, 46.13) * mm, "end": v(-10.7, 43.7) * mm});
            skLineSegment(sketch, "E30.6.79.0", {"start": v(-11.81, 46) * mm, "end": v(-11.33, 46.13) * mm});
            skLineSegment(sketch, "E30.9.79.0", {"start": v(-11.81, 46) * mm, "end": v(-12.3, 45.88) * mm});
            skLineSegment(sketch, "E30.1.80.0", {"start": v(-15.15, 45.02) * mm, "end": v(-14.38, 42.64) * mm});
            skLineSegment(sketch, "E30.3.80.0", {"start": v(-14.2, 45.33) * mm, "end": v(-13.43, 42.95) * mm});
            skLineSegment(sketch, "E30.6.80.0", {"start": v(-14.68, 45.18) * mm, "end": v(-14.2, 45.33) * mm});
            skLineSegment(sketch, "E30.9.80.0", {"start": v(-14.68, 45.18) * mm, "end": v(-15.15, 45.02) * mm});
            skLineSegment(sketch, "E30.1.81.0", {"start": v(-17.95, 43.98) * mm, "end": v(-17.03, 41.65) * mm});
            skLineSegment(sketch, "E30.3.81.0", {"start": v(-17.02, 44.35) * mm, "end": v(-16.1, 42.02) * mm});
            skLineSegment(sketch, "E30.6.81.0", {"start": v(-17.49, 44.16) * mm, "end": v(-17.02, 44.35) * mm});
            skLineSegment(sketch, "E30.9.81.0", {"start": v(-17.49, 44.16) * mm, "end": v(-17.95, 43.98) * mm});
            skLineSegment(sketch, "E30.1.82.0", {"start": v(-20.68, 42.77) * mm, "end": v(-19.61, 40.5) * mm});
            skLineSegment(sketch, "E30.3.82.0", {"start": v(-19.77, 43.2) * mm, "end": v(-18.7, 40.93) * mm});
            skLineSegment(sketch, "E30.6.82.0", {"start": v(-20.22, 42.98) * mm, "end": v(-19.77, 43.2) * mm});
            skLineSegment(sketch, "E30.9.82.0", {"start": v(-20.22, 42.98) * mm, "end": v(-20.68, 42.77) * mm});
            skLineSegment(sketch, "E30.1.83.0", {"start": v(-23.32, 41.38) * mm, "end": v(-22.12, 39.2) * mm});
            skLineSegment(sketch, "E30.3.83.0", {"start": v(-22.45, 41.87) * mm, "end": v(-21.24, 39.67) * mm});
            skLineSegment(sketch, "E30.6.83.0", {"start": v(-22.88, 41.62) * mm, "end": v(-22.45, 41.87) * mm});
            skLineSegment(sketch, "E30.9.83.0", {"start": v(-22.88, 41.62) * mm, "end": v(-23.32, 41.38) * mm});
            skLineSegment(sketch, "E30.1.84.0", {"start": v(-25.87, 39.84) * mm, "end": v(-24.53, 37.72) * mm});
            skLineSegment(sketch, "E30.3.84.0", {"start": v(-25.03, 40.37) * mm, "end": v(-23.69, 38.26) * mm});
            skLineSegment(sketch, "E30.6.84.0", {"start": v(-25.45, 40.1) * mm, "end": v(-25.03, 40.37) * mm});
            skLineSegment(sketch, "E30.9.84.0", {"start": v(-25.45, 40.1) * mm, "end": v(-25.87, 39.84) * mm});
            skLineSegment(sketch, "E30.1.85.0", {"start": v(-28.32, 38.13) * mm, "end": v(-26.85, 36.1) * mm});
            skLineSegment(sketch, "E30.3.85.0", {"start": v(-27.52, 38.72) * mm, "end": v(-26.04, 36.7) * mm});
            skLineSegment(sketch, "E30.6.85.0", {"start": v(-27.92, 38.43) * mm, "end": v(-27.52, 38.72) * mm});
            skLineSegment(sketch, "E30.9.85.0", {"start": v(-27.92, 38.43) * mm, "end": v(-28.32, 38.13) * mm});
            skLineSegment(sketch, "E30.1.86.0", {"start": v(-30.66, 36.28) * mm, "end": v(-29.07, 34.35) * mm});
            skLineSegment(sketch, "E30.3.86.0", {"start": v(-29.9, 36.92) * mm, "end": v(-28.3, 34.99) * mm});
            skLineSegment(sketch, "E30.6.86.0", {"start": v(-30.28, 36.6) * mm, "end": v(-29.9, 36.92) * mm});
            skLineSegment(sketch, "E30.9.86.0", {"start": v(-30.28, 36.6) * mm, "end": v(-30.66, 36.28) * mm});
            skLineSegment(sketch, "E30.1.87.0", {"start": v(-32.88, 34.28) * mm, "end": v(-31.17, 32.46) * mm});
            skLineSegment(sketch, "E30.3.87.0", {"start": v(-32.15, 34.97) * mm, "end": v(-30.44, 33.14) * mm});
            skLineSegment(sketch, "E30.6.87.0", {"start": v(-32.52, 34.63) * mm, "end": v(-32.15, 34.97) * mm});
            skLineSegment(sketch, "E30.9.87.0", {"start": v(-32.52, 34.63) * mm, "end": v(-32.88, 34.28) * mm});
            skLineSegment(sketch, "E30.1.88.0", {"start": v(-34.97, 32.15) * mm, "end": v(-33.14, 30.44) * mm});
            skLineSegment(sketch, "E30.3.88.0", {"start": v(-34.28, 32.88) * mm, "end": v(-32.46, 31.17) * mm});
            skLineSegment(sketch, "E30.6.88.0", {"start": v(-34.63, 32.52) * mm, "end": v(-34.28, 32.88) * mm});
            skLineSegment(sketch, "E30.9.88.0", {"start": v(-34.63, 32.52) * mm, "end": v(-34.97, 32.15) * mm});
            skLineSegment(sketch, "E30.1.89.0", {"start": v(-36.92, 29.9) * mm, "end": v(-34.99, 28.3) * mm});
            skLineSegment(sketch, "E30.3.89.0", {"start": v(-36.28, 30.66) * mm, "end": v(-34.35, 29.07) * mm});
            skLineSegment(sketch, "E30.6.89.0", {"start": v(-36.6, 30.28) * mm, "end": v(-36.28, 30.66) * mm});
            skLineSegment(sketch, "E30.9.89.0", {"start": v(-36.6, 30.28) * mm, "end": v(-36.92, 29.9) * mm});
            skLineSegment(sketch, "E30.1.90.0", {"start": v(-38.72, 27.52) * mm, "end": v(-36.7, 26.04) * mm});
            skLineSegment(sketch, "E30.3.90.0", {"start": v(-38.13, 28.32) * mm, "end": v(-36.1, 26.85) * mm});
            skLineSegment(sketch, "E30.6.90.0", {"start": v(-38.43, 27.92) * mm, "end": v(-38.13, 28.32) * mm});
            skLineSegment(sketch, "E30.9.90.0", {"start": v(-38.43, 27.92) * mm, "end": v(-38.72, 27.52) * mm});
            skLineSegment(sketch, "E30.1.91.0", {"start": v(-40.37, 25.03) * mm, "end": v(-38.26, 23.69) * mm});
            skLineSegment(sketch, "E30.3.91.0", {"start": v(-39.84, 25.87) * mm, "end": v(-37.72, 24.53) * mm});
            skLineSegment(sketch, "E30.6.91.0", {"start": v(-40.1, 25.45) * mm, "end": v(-39.84, 25.87) * mm});
            skLineSegment(sketch, "E30.9.91.0", {"start": v(-40.1, 25.45) * mm, "end": v(-40.37, 25.03) * mm});
            skLineSegment(sketch, "E30.1.92.0", {"start": v(-41.87, 22.45) * mm, "end": v(-39.67, 21.24) * mm});
            skLineSegment(sketch, "E30.3.92.0", {"start": v(-41.38, 23.32) * mm, "end": v(-39.2, 22.12) * mm});
            skLineSegment(sketch, "E30.6.92.0", {"start": v(-41.62, 22.88) * mm, "end": v(-41.38, 23.32) * mm});
            skLineSegment(sketch, "E30.9.92.0", {"start": v(-41.62, 22.88) * mm, "end": v(-41.87, 22.45) * mm});
            skLineSegment(sketch, "E30.1.93.0", {"start": v(-43.2, 19.77) * mm, "end": v(-40.93, 18.7) * mm});
            skLineSegment(sketch, "E30.3.93.0", {"start": v(-42.77, 20.68) * mm, "end": v(-40.5, 19.61) * mm});
            skLineSegment(sketch, "E30.6.93.0", {"start": v(-42.98, 20.22) * mm, "end": v(-42.77, 20.68) * mm});
            skLineSegment(sketch, "E30.9.93.0", {"start": v(-42.98, 20.22) * mm, "end": v(-43.2, 19.77) * mm});
            skLineSegment(sketch, "E30.1.94.0", {"start": v(-44.35, 17.02) * mm, "end": v(-42.02, 16.1) * mm});
            skLineSegment(sketch, "E30.3.94.0", {"start": v(-43.98, 17.95) * mm, "end": v(-41.65, 17.03) * mm});
            skLineSegment(sketch, "E30.6.94.0", {"start": v(-44.16, 17.49) * mm, "end": v(-43.98, 17.95) * mm});
            skLineSegment(sketch, "E30.9.94.0", {"start": v(-44.16, 17.49) * mm, "end": v(-44.35, 17.02) * mm});
            skLineSegment(sketch, "E30.1.95.0", {"start": v(-45.33, 14.2) * mm, "end": v(-42.95, 13.43) * mm});
            skLineSegment(sketch, "E30.3.95.0", {"start": v(-45.02, 15.15) * mm, "end": v(-42.64, 14.38) * mm});
            skLineSegment(sketch, "E30.6.95.0", {"start": v(-45.18, 14.68) * mm, "end": v(-45.02, 15.15) * mm});
            skLineSegment(sketch, "E30.9.95.0", {"start": v(-45.18, 14.68) * mm, "end": v(-45.33, 14.2) * mm});
            skLineSegment(sketch, "E30.1.96.0", {"start": v(-46.13, 11.33) * mm, "end": v(-43.7, 10.7) * mm});
            skLineSegment(sketch, "E30.3.96.0", {"start": v(-45.88, 12.3) * mm, "end": v(-43.46, 11.67) * mm});
            skLineSegment(sketch, "E30.6.96.0", {"start": v(-46, 11.81) * mm, "end": v(-45.88, 12.3) * mm});
            skLineSegment(sketch, "E30.9.96.0", {"start": v(-46, 11.81) * mm, "end": v(-46.13, 11.33) * mm});
            skLineSegment(sketch, "E30.1.97.0", {"start": v(-46.75, 8.4) * mm, "end": v(-44.3, 7.94) * mm});
            skLineSegment(sketch, "E30.3.97.0", {"start": v(-46.56, 9.4) * mm, "end": v(-44.1, 8.92) * mm});
            skLineSegment(sketch, "E30.6.97.0", {"start": v(-46.66, 8.9) * mm, "end": v(-46.56, 9.4) * mm});
            skLineSegment(sketch, "E30.9.97.0", {"start": v(-46.66, 8.9) * mm, "end": v(-46.75, 8.4) * mm});
            skLineSegment(sketch, "E30.1.98.0", {"start": v(-47.19, 5.46) * mm, "end": v(-44.7, 5.14) * mm});
            skLineSegment(sketch, "E30.3.98.0", {"start": v(-47.06, 6.45) * mm, "end": v(-44.58, 6.14) * mm});
            skLineSegment(sketch, "E30.6.98.0", {"start": v(-47.13, 5.95) * mm, "end": v(-47.06, 6.45) * mm});
            skLineSegment(sketch, "E30.9.98.0", {"start": v(-47.13, 5.95) * mm, "end": v(-47.19, 5.46) * mm});
            skLineSegment(sketch, "E30.1.99.0", {"start": v(-47.44, 2.48) * mm, "end": v(-44.94, 2.33) * mm});
            skLineSegment(sketch, "E30.3.99.0", {"start": v(-47.37, 3.48) * mm, "end": v(-44.88, 3.32) * mm});
            skLineSegment(sketch, "E30.6.99.0", {"start": v(-47.4, 2.98) * mm, "end": v(-47.37, 3.48) * mm});
            skLineSegment(sketch, "E30.9.99.0", {"start": v(-47.4, 2.98) * mm, "end": v(-47.44, 2.48) * mm});
            skLineSegment(sketch, "E31", {"start": v(0, 0) * mm, "end": v(0, 2.6) * mm});
            skLineSegment(sketch, "E32", {"start": v(0, 2.6) * mm, "end": v(1.3, 2.6) * mm});
            skLineSegment(sketch, "E33", {"start": v(1.3, 2.6) * mm, "end": v(1.3, 1.3) * mm});
            skLineSegment(sketch, "E34", {"start": v(1.3, 1.3) * mm, "end": v(2.7, 1.3) * mm});
            skLineSegment(sketch, "E35", {"start": v(2.7, 1.3) * mm, "end": v(2.7, 0) * mm});
            skLineSegment(sketch, "E36.MirrorCS", {"start": v(0, 2.6) * mm, "end": v(-1.3, 2.6) * mm});
            skLineSegment(sketch, "E37.MirrorCS", {"start": v(-1.3, 2.6) * mm, "end": v(-1.3, 1.3) * mm});
            skLineSegment(sketch, "E38.MirrorCS", {"start": v(-1.3, 1.3) * mm, "end": v(-2.7, 1.3) * mm});
            skLineSegment(sketch, "E39.MirrorCS", {"start": v(-2.7, 1.3) * mm, "end": v(-2.7, 0) * mm});
            skLineSegment(sketch, "E40.MirrorCS", {"start": v(-2.7, -1.3) * mm, "end": v(-2.7, 0) * mm});
            skLineSegment(sketch, "E41.MirrorCS", {"start": v(-1.3, -1.3) * mm, "end": v(-2.7, -1.3) * mm});
            skLineSegment(sketch, "E42.MirrorCS", {"start": v(-1.3, -2.6) * mm, "end": v(-1.3, -1.3) * mm});
            skLineSegment(sketch, "E43.MirrorCS", {"start": v(0, -2.6) * mm, "end": v(-1.3, -2.6) * mm});
            skLineSegment(sketch, "E44.MirrorCS", {"start": v(0, -2.6) * mm, "end": v(1.3, -2.6) * mm});
            skLineSegment(sketch, "E45.MirrorCS", {"start": v(1.3, -2.6) * mm, "end": v(1.3, -1.3) * mm});
            skLineSegment(sketch, "E46.MirrorCS", {"start": v(1.3, -1.3) * mm, "end": v(2.7, -1.3) * mm});
            skLineSegment(sketch, "E47.MirrorCS", {"start": v(2.7, -1.3) * mm, "end": v(2.7, 0) * mm});
            skSolve(sketch);
        }
        {
            var Q0;
            Q0 = qSketchRegion(id + "F0", true);
            extrude(context, id + "F1", {"entities" : qUnion([Q0]), "depth" : 3 * mm});
        }
    });
